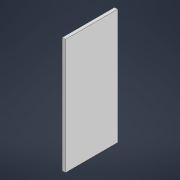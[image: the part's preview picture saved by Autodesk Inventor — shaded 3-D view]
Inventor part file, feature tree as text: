
AUTODESK INVENTOR PART (.ipt)
format: ipt  version: 2022 (Build 260153000, 153)  size: 206,848 bytes
history: native  units: in
note: dims shown in document units (in); Inventor stores cm internally (conversion verified against a paired STEP export)
features: other x3, extrude x1, sketch x1, reference x1
ambient origin geometry x8: Origin, YZ Plane, XZ Plane, XY Plane, X Axis, Y Axis, Z Axis, Center Point
bodies: Solid1 (feature_tree)
feature tree (6):
  extrude  "Extrusion1"  Depth=1.0in TaperAngle=0.0deg
  sketch  "Sketch1"  dims[d0=0.02in d1=1.0in d2=0.0in]
  reference  "Reference1"
  parser-record x1  (decoder bookkeeping rows leaked as tree rows — omitted from the tree; the rows remain in map.json)
  other  "Prototype Assembly.iam"
  other  "Base:1"
note: 1 file-system path scrubbed to <path> (originals preserved in map.json)
